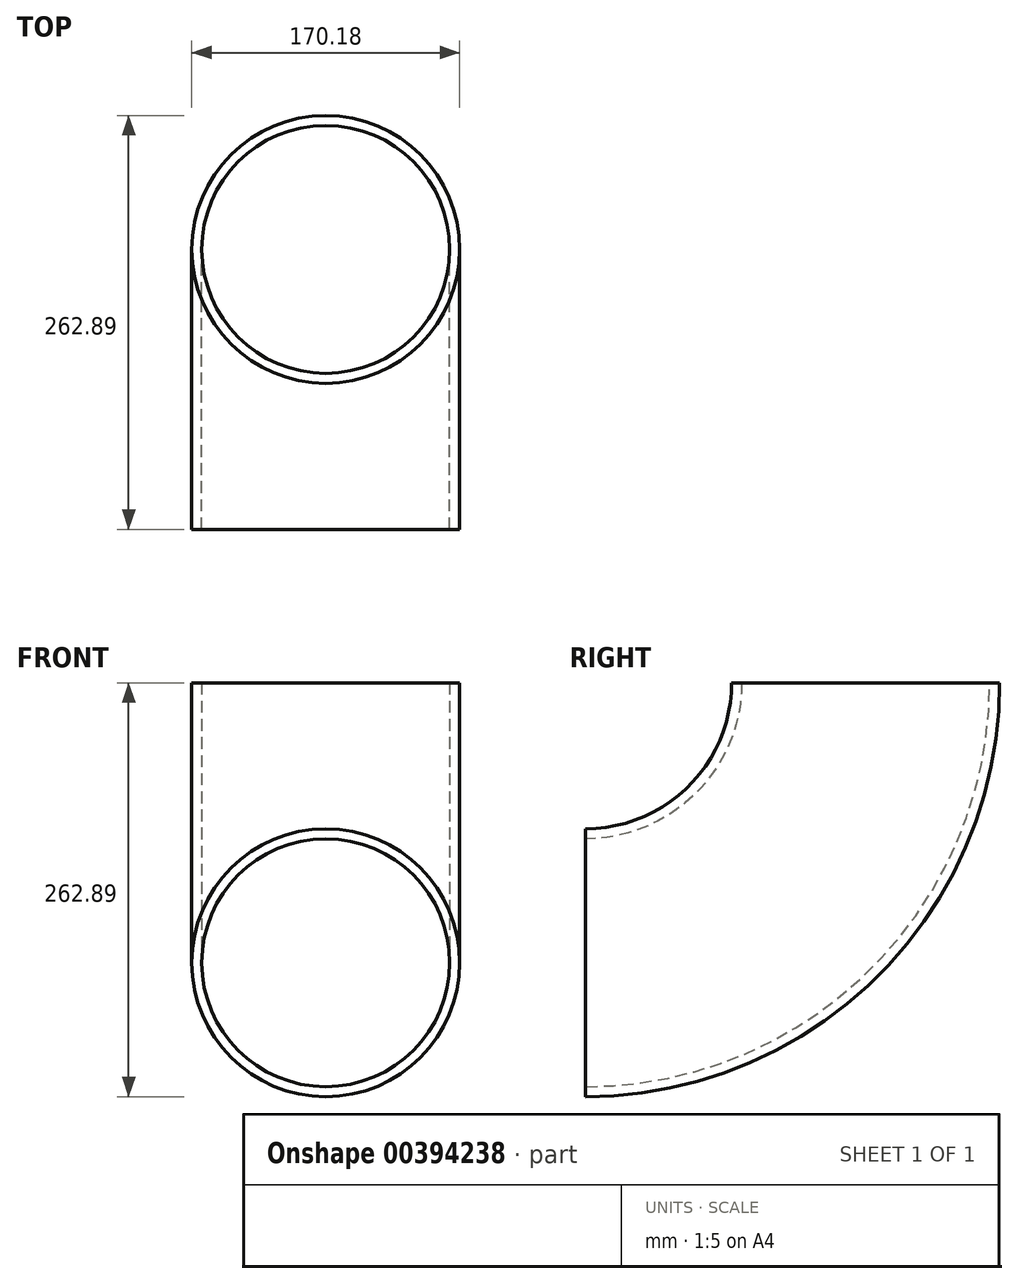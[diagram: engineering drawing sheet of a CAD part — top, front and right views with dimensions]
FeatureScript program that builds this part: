
annotation { "Feature Type Name" : "Feature", "Feature Type Description" : "" }
export const myFeature = defineFeature(function(context is Context, id is Id, definition is map)
    precondition{}
    {
        {
            var Q0;
            Q0=qCreatedBy(makeId("Front.planeOp"),FACE);
            var sketch = newSketch(context, id + "F0", { "sketchPlane" : qUnion([Q0])});
            skCircle(sketch, "E0", {"center": v(0, 0) * mm, "radius": 85.1 * mm});
            skCircle(sketch, "E1", {"center": v(0, 0) * mm, "radius": 78.74 * mm});
            skSolve(sketch);
        }
        {
            var Q0;
            Q0=qCreatedBy(makeId("Right.planeOp"),FACE);
            var sketch = newSketch(context, id + "F1", { "sketchPlane" : qUnion([Q0])});
            skLineSegment(sketch, "E2", {"start": v(0, 0) * mm, "end": v(177.8, 0) * mm, "construction": true});
            skLineSegment(sketch, "E3", {"start": v(177.8, 0) * mm, "end": v(177.8, 177.8) * mm, "construction": true});
            skArc(sketch, "E4", {"start": v(0, 0) * mm, "mid": v(125.72, 52.08) * mm, "end": v(177.8, 177.8) * mm});
            skSolve(sketch);
        }
        {
            var Q0;
            Q0=makeQuery(id+"F0.imprint","IMPRINT",FACE,{"disambiguationData":[TD([[makeQuery(id+"F0.imprint","IMPRINT",EDGE,{"derivedFrom":sQuery(id+"F0.wireOp",EDGE,"E0")}),1.0]])]});
            var Q1;
            Q1=sQuery(id+"F1.wireOp",EDGE,"E4");
            sweep(context, id + "F2", {"profiles" : qUnion([Q0]), "path" : qUnion([Q1])});
        }
    });
